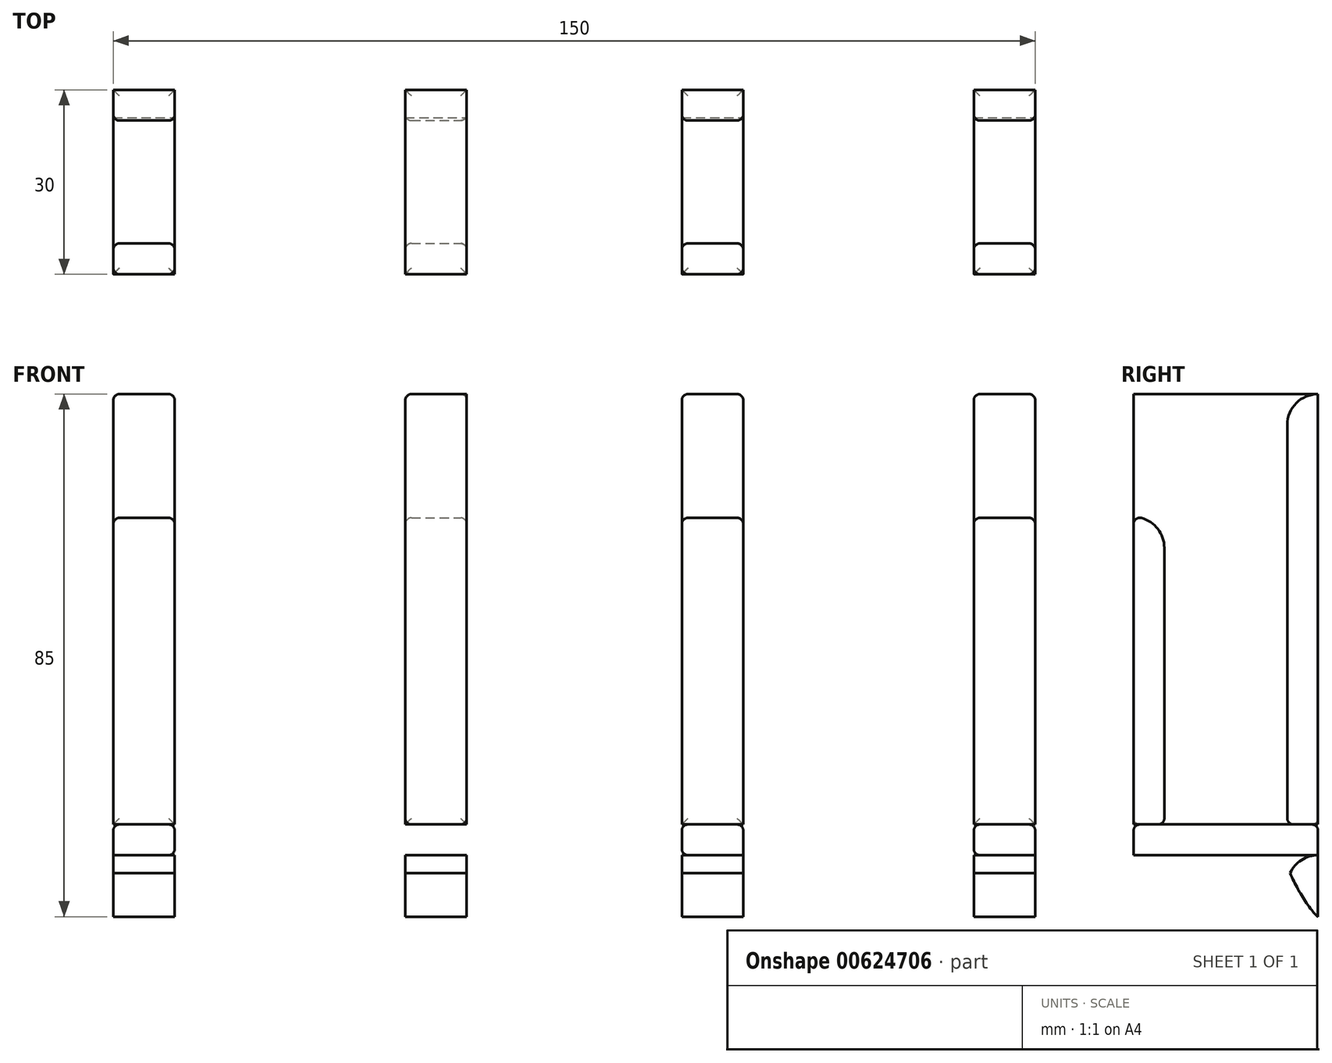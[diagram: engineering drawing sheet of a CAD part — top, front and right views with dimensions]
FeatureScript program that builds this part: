
annotation { "Feature Type Name" : "Feature", "Feature Type Description" : "" }
export const myFeature = defineFeature(function(context is Context, id is Id, definition is map)
    precondition{}
    {
        {
            var Q0;
            Q0=qCreatedBy(makeId("Front.planeOp"),FACE);
            var sketch = newSketch(context, id + "F0", { "sketchPlane" : qUnion([Q0])});
            skLineSegment(sketch, "E0.bottom", {"start": v(-75, 75) * mm, "end": v(-65, 75) * mm});
            skLineSegment(sketch, "E0.top", {"start": v(-75, 0) * mm, "end": v(-65, 0) * mm});
            skLineSegment(sketch, "E0.left", {"start": v(-75, 75) * mm, "end": v(-75, 0) * mm});
            skLineSegment(sketch, "E0.right", {"start": v(-65, 75) * mm, "end": v(-65, 0) * mm});
            skLineSegment(sketch, "E1.bottom", {"start": v(-27.5, 75) * mm, "end": v(-17.5, 75) * mm});
            skLineSegment(sketch, "E1.top", {"start": v(-27.5, 0) * mm, "end": v(-17.5, 0) * mm});
            skLineSegment(sketch, "E1.left", {"start": v(-27.5, 75) * mm, "end": v(-27.5, 0) * mm});
            skLineSegment(sketch, "E1.right", {"start": v(-17.5, 75) * mm, "end": v(-17.5, 0) * mm});
            skLineSegment(sketch, "E2.bottom", {"start": v(17.5, 75) * mm, "end": v(27.5, 75) * mm});
            skLineSegment(sketch, "E2.top", {"start": v(17.5, 0) * mm, "end": v(27.5, 0) * mm});
            skLineSegment(sketch, "E2.left", {"start": v(17.5, 75) * mm, "end": v(17.5, 0) * mm});
            skLineSegment(sketch, "E2.right", {"start": v(27.5, 75) * mm, "end": v(27.5, 0) * mm});
            skLineSegment(sketch, "E3.bottom", {"start": v(65, 75) * mm, "end": v(75, 75) * mm});
            skLineSegment(sketch, "E3.top", {"start": v(65, 0) * mm, "end": v(75, 0) * mm});
            skLineSegment(sketch, "E3.left", {"start": v(65, 75) * mm, "end": v(65, 0) * mm});
            skLineSegment(sketch, "E3.right", {"start": v(75, 75) * mm, "end": v(75, 0) * mm});
            skLineSegment(sketch, "E4", {"start": v(-75, 0) * mm, "end": v(75, 0) * mm});
            skLineSegment(sketch, "E5", {"start": v(-75, 0) * mm, "end": v(0, 0) * mm});
            skLineSegment(sketch, "E6", {"start": v(-65, 0) * mm, "end": v(-27.5, 0) * mm});
            skLineSegment(sketch, "E7", {"start": v(-75, 5) * mm, "end": v(75, 5) * mm});
            skLineSegment(sketch, "E8.top", {"start": v(-75, -10) * mm, "end": v(-65, -10) * mm});
            skLineSegment(sketch, "E8.left", {"start": v(-75, 0) * mm, "end": v(-75, -10) * mm});
            skLineSegment(sketch, "E8.right", {"start": v(-65, 0) * mm, "end": v(-65, -10) * mm});
            skLineSegment(sketch, "E9.top", {"start": v(-27.5, -10) * mm, "end": v(-17.5, -10) * mm});
            skLineSegment(sketch, "E9.left", {"start": v(-27.5, 0) * mm, "end": v(-27.5, -10) * mm});
            skLineSegment(sketch, "E9.right", {"start": v(-17.5, 0) * mm, "end": v(-17.5, -10) * mm});
            skLineSegment(sketch, "E10.top", {"start": v(17.5, -10) * mm, "end": v(27.5, -10) * mm});
            skLineSegment(sketch, "E10.left", {"start": v(17.5, 0) * mm, "end": v(17.5, -10) * mm});
            skLineSegment(sketch, "E10.right", {"start": v(27.5, 0) * mm, "end": v(27.5, -10) * mm});
            skLineSegment(sketch, "E11.top", {"start": v(65, -10) * mm, "end": v(75, -10) * mm});
            skLineSegment(sketch, "E11.left", {"start": v(65, 0) * mm, "end": v(65, -10) * mm});
            skLineSegment(sketch, "E11.right", {"start": v(75, 0) * mm, "end": v(75, -10) * mm});
            skSolve(sketch);
        }
        {
            var Q0;
            Q0=makeQuery(id+"F0.imprint","IMPRINT",FACE,{"disambiguationData":[TD([[makeQuery(id+"F0.imprint","IMPRINT",EDGE,{"derivedFrom":sQuery(id+"F0.wireOp",EDGE,"E0.bottom")}),-1.0]])]});
            var Q1;
            Q1=makeQuery(id+"F0.imprint","IMPRINT",FACE,{"disambiguationData":[TD([[makeQuery(id+"F0.imprint","IMPRINT",EDGE,{"derivedFrom":sQuery(id+"F0.wireOp",EDGE,"E1.bottom")}),-1.0]])]});
            var Q2;
            Q2=makeQuery(id+"F0.imprint","IMPRINT",FACE,{"disambiguationData":[TD([[makeQuery(id+"F0.imprint","IMPRINT",EDGE,{"derivedFrom":sQuery(id+"F0.wireOp",EDGE,"E2.bottom")}),-1.0]])]});
            var Q3;
            Q3=makeQuery(id+"F0.imprint","IMPRINT",FACE,{"disambiguationData":[TD([[makeQuery(id+"F0.imprint","IMPRINT",EDGE,{"derivedFrom":sQuery(id+"F0.wireOp",EDGE,"E3.bottom")}),-1.0]])]});
            var Q4;
            Q4=makeQuery(id+"F0.imprint","IMPRINT",FACE,{"disambiguationData":[TD([[makeQuery(id+"F0.imprint","IMPRINT",EDGE,{"derivedFrom":sQuery(id+"F0.wireOp",EDGE,"E0.top")}),-1.0]])]});
            var Q5;
            Q5=makeQuery(id+"F0.imprint","IMPRINT",FACE,{"disambiguationData":[TD([[makeQuery(id+"F0.imprint","IMPRINT",EDGE,{"derivedFrom":sQuery(id+"F0.wireOp",EDGE,"E1.top")}),-1.0]])]});
            var Q6;
            Q6=makeQuery(id+"F0.imprint","IMPRINT",FACE,{"disambiguationData":[TD([[makeQuery(id+"F0.imprint","IMPRINT",EDGE,{"derivedFrom":sQuery(id+"F0.wireOp",EDGE,"E2.top")}),-1.0]])]});
            var Q7;
            Q7=makeQuery(id+"F0.imprint","IMPRINT",FACE,{"disambiguationData":[TD([[makeQuery(id+"F0.imprint","IMPRINT",EDGE,{"derivedFrom":sQuery(id+"F0.wireOp",EDGE,"E3.top")}),-1.0]])]});
            extrude(context, id + "F1", {"entities" : qUnion([Q0, Q1, Q2, Q3, Q4, Q5, Q6, Q7]), "depth" : 5 * mm, "offsetDistance" : 25 * mm});
        }
        {
            var Q0;
            {var subQ0=sQuery(id+"F0.wireOp",EDGE,"E5");var subQ5=sQuery(id+"F0.wireOp",EDGE,"E1.right");var subQ6=makeQuery(id+"F0.imprint","INTERSECT",VERTEX,{"derivedFrom":[subQ5,subQ0]});Q0=makeQuery(id+"F0.imprint","IMPRINT",FACE,{"disambiguationData":[TD([[makeQuery(id+"F0.imprint","IMPRINT",EDGE,{"disambiguationData":[TD([[subQ6,1.0]])],"derivedFrom":subQ5}),-1.0]])]});}
            var Q1;
            {var subQ0=sQuery(id+"F0.wireOp",EDGE,"E4");var subQ1=sQuery(id+"F0.wireOp",EDGE,"E2.left");var subQ2=makeQuery(id+"F0.imprint","INTERSECT",VERTEX,{"derivedFrom":[subQ1,subQ0]});Q1=makeQuery(id+"F0.imprint","IMPRINT",FACE,{"disambiguationData":[TD([[makeQuery(id+"F0.imprint","IMPRINT",EDGE,{"disambiguationData":[TD([[subQ2,1.0]])],"derivedFrom":subQ1}),1.0]])]});}
            var Q2;
            {var subQ0=sQuery(id+"F0.wireOp",EDGE,"E4");var subQ1=sQuery(id+"F0.wireOp",EDGE,"E3.left");var subQ2=makeQuery(id+"F0.imprint","INTERSECT",VERTEX,{"derivedFrom":[subQ1,subQ0]});Q2=makeQuery(id+"F0.imprint","IMPRINT",FACE,{"disambiguationData":[TD([[makeQuery(id+"F0.imprint","IMPRINT",EDGE,{"disambiguationData":[TD([[subQ2,1.0]])],"derivedFrom":subQ1}),1.0]])]});}
            var Q3;
            {var subQ0=sQuery(id+"F0.wireOp",EDGE,"E0.top");Q3=makeQuery(id+"F0.imprint","IMPRINT",FACE,{"disambiguationData":[TD([[makeQuery(id+"F0.imprint","IMPRINT",EDGE,{"derivedFrom":subQ0}),1.0]])]});}
            extrude(context, id + "F2", {"entities" : qUnion([Q0, Q1, Q2, Q3]), "depth" : (5 + 20 + 5) * mm, "offsetDistance" : 25 * mm});
        }
        {
            var Q0;
            {var subQ0=sQuery(id+"F0.wireOp",EDGE,"E7");Q0=makeQuery(id+"F2.opExtrude","SWEPT_FACE",FACE,{"disambiguationData":[OSD([subQ0]),TDD([makeQuery(id+"F0.imprint","IMPRINT",EDGE,{"disambiguationData":[TD([[makeQuery(id+"F0.imprint","INTERSECT",VERTEX,{"derivedFrom":[sQuery(id+"F0.wireOp",EDGE,"E0.left"),subQ0]}),-1.0]])],"derivedFrom":subQ0})])]});}
            var sketch = newSketch(context, id + "F3", { "sketchPlane" : qUnion([Q0])});
            skLineSegment(sketch, "E12.bottom", {"start": v(-27.5, -25) * mm, "end": v(-17.5, -25) * mm});
            skLineSegment(sketch, "E12.top", {"start": v(-27.5, -30) * mm, "end": v(-17.5, -30) * mm});
            skLineSegment(sketch, "E12.left", {"start": v(-27.5, -25) * mm, "end": v(-27.5, -30) * mm});
            skLineSegment(sketch, "E12.right", {"start": v(-17.5, -25) * mm, "end": v(-17.5, -30) * mm});
            skLineSegment(sketch, "E13.bottom", {"start": v(17.5, -25) * mm, "end": v(27.5, -25) * mm});
            skLineSegment(sketch, "E13.top", {"start": v(17.5, -30) * mm, "end": v(27.5, -30) * mm});
            skLineSegment(sketch, "E13.left", {"start": v(17.5, -25) * mm, "end": v(17.5, -30) * mm});
            skLineSegment(sketch, "E13.right", {"start": v(27.5, -25) * mm, "end": v(27.5, -30) * mm});
            skLineSegment(sketch, "E14.bottom", {"start": v(65, -25) * mm, "end": v(75, -25) * mm});
            skLineSegment(sketch, "E14.top", {"start": v(65, -30) * mm, "end": v(75, -30) * mm});
            skLineSegment(sketch, "E14.left", {"start": v(65, -25) * mm, "end": v(65, -30) * mm});
            skLineSegment(sketch, "E14.right", {"start": v(75, -25) * mm, "end": v(75, -30) * mm});
            skLineSegment(sketch, "E15.bottom", {"start": v(-75, -30) * mm, "end": v(-65, -30) * mm});
            skLineSegment(sketch, "E15.top", {"start": v(-75, -25) * mm, "end": v(-65, -25) * mm});
            skLineSegment(sketch, "E15.left", {"start": v(-75, -30) * mm, "end": v(-75, -25) * mm});
            skLineSegment(sketch, "E15.right", {"start": v(-65, -30) * mm, "end": v(-65, -25) * mm});
            skSolve(sketch);
        }
        {
            var Q0;
            Q0 = qSketchRegion(id + "F3", true);
            extrude(context, id + "F4", {"entities" : qUnion([Q0]), "depth" : 50 * mm, "offsetDistance" : 25 * mm});
        }
        {
            var Q0;
            Q0=makeQuery(id+"F1.opExtrude","SWEPT_BODY",BODY,{"disambiguationData":[OSD([sQuery(id+"F0.wireOp",EDGE,"E0.bottom"),sQuery(id+"F0.wireOp",EDGE,"E0.left"),sQuery(id+"F0.wireOp",EDGE,"E0.right"),sQuery(id+"F0.wireOp",EDGE,"E7")])]});
            var Q1;
            Q1=makeQuery(id+"F1.opExtrude","SWEPT_BODY",BODY,{"disambiguationData":[OSD([sQuery(id+"F0.wireOp",EDGE,"E1.bottom"),sQuery(id+"F0.wireOp",EDGE,"E1.left"),sQuery(id+"F0.wireOp",EDGE,"E1.right"),sQuery(id+"F0.wireOp",EDGE,"E7")])]});
            var Q2;
            Q2=makeQuery(id+"F1.opExtrude","SWEPT_BODY",BODY,{"disambiguationData":[OSD([sQuery(id+"F0.wireOp",EDGE,"E2.bottom"),sQuery(id+"F0.wireOp",EDGE,"E2.left"),sQuery(id+"F0.wireOp",EDGE,"E2.right"),sQuery(id+"F0.wireOp",EDGE,"E7")])]});
            var Q3;
            Q3=makeQuery(id+"F1.opExtrude","SWEPT_BODY",BODY,{"disambiguationData":[OSD([sQuery(id+"F0.wireOp",EDGE,"E3.bottom"),sQuery(id+"F0.wireOp",EDGE,"E3.left"),sQuery(id+"F0.wireOp",EDGE,"E3.right"),sQuery(id+"F0.wireOp",EDGE,"E7")])]});
            var Q4;
            Q4=makeQuery(id+"F4.opExtrude","SWEPT_BODY",BODY,{"disambiguationData":[OSD([sQuery(id+"F3.wireOp",EDGE,"E12.bottom"),sQuery(id+"F3.wireOp",EDGE,"E12.top"),sQuery(id+"F3.wireOp",EDGE,"E12.left"),sQuery(id+"F3.wireOp",EDGE,"E12.right")])]});
            var Q5;
            Q5=makeQuery(id+"F4.opExtrude","SWEPT_BODY",BODY,{"disambiguationData":[OSD([sQuery(id+"F3.wireOp",EDGE,"E13.bottom"),sQuery(id+"F3.wireOp",EDGE,"E13.top"),sQuery(id+"F3.wireOp",EDGE,"E13.left"),sQuery(id+"F3.wireOp",EDGE,"E13.right")])]});
            var Q6;
            Q6=makeQuery(id+"F4.opExtrude","SWEPT_BODY",BODY,{"disambiguationData":[OSD([sQuery(id+"F3.wireOp",EDGE,"E14.bottom"),sQuery(id+"F3.wireOp",EDGE,"E14.top"),sQuery(id+"F3.wireOp",EDGE,"E14.left"),sQuery(id+"F3.wireOp",EDGE,"E14.right")])]});
            var Q7;
            Q7=makeQuery(id+"F4.opExtrude","SWEPT_BODY",BODY,{"disambiguationData":[OSD([sQuery(id+"F3.wireOp",EDGE,"E15.bottom"),sQuery(id+"F3.wireOp",EDGE,"E15.top"),sQuery(id+"F3.wireOp",EDGE,"E15.left"),sQuery(id+"F3.wireOp",EDGE,"E15.right")])]});
            booleanBodies(context, id + "F5", {"operationType" : BooleanOperationType.UNION, "tools" : qUnion([Q0, Q1, Q2, Q3, Q4, Q5, Q6, Q7])});
        }
        {
            var Q0;
            Q0=makeQuery(id+"F1.opExtrude","CAP_EDGE",EDGE,{"disambiguationData":[OSD([sQuery(id+"F0.wireOp",EDGE,"E0.bottom")])],"isStart":false});
            var Q1;
            Q1=makeQuery(id+"F1.opExtrude","CAP_EDGE",EDGE,{"disambiguationData":[OSD([sQuery(id+"F0.wireOp",EDGE,"E1.bottom")])],"isStart":false});
            var Q2;
            Q2=makeQuery(id+"F1.opExtrude","CAP_EDGE",EDGE,{"disambiguationData":[OSD([sQuery(id+"F0.wireOp",EDGE,"E2.bottom")])],"isStart":false});
            var Q3;
            Q3=makeQuery(id+"F1.opExtrude","CAP_EDGE",EDGE,{"disambiguationData":[OSD([sQuery(id+"F0.wireOp",EDGE,"E3.bottom")])],"isStart":false});
            fillet(context, id + "F6", {"entities" : qUnion([Q0, Q1, Q2, Q3]), "radius" : 5 * mm, "tangentPropagation" : true, "allowEdgeOverflow" : false});
        }
        {
            var Q0;
            Q0=makeQuery(id+"F4.opExtrude","CAP_EDGE",EDGE,{"disambiguationData":[OSD([sQuery(id+"F3.wireOp",EDGE,"E15.top")])],"isStart":false});
            var Q1;
            Q1=makeQuery(id+"F4.opExtrude","CAP_EDGE",EDGE,{"disambiguationData":[OSD([sQuery(id+"F3.wireOp",EDGE,"E12.bottom")])],"isStart":false});
            var Q2;
            Q2=makeQuery(id+"F4.opExtrude","CAP_EDGE",EDGE,{"disambiguationData":[OSD([sQuery(id+"F3.wireOp",EDGE,"E13.bottom")])],"isStart":false});
            var Q3;
            Q3=makeQuery(id+"F4.opExtrude","CAP_EDGE",EDGE,{"disambiguationData":[OSD([sQuery(id+"F3.wireOp",EDGE,"E14.bottom")])],"isStart":false});
            fillet(context, id + "F7", {"entities" : qUnion([Q0, Q1, Q2, Q3]), "radius" : 5 * mm, "tangentPropagation" : true, "allowEdgeOverflow" : false});
        }
        {
            var Q0;
            Q0=makeQuery(id+"F7.opFillet","BLEND_EDGE",EDGE,{"blendedFrom":[makeQuery(id+"F4.opExtrude","CAP_EDGE",EDGE,{"disambiguationData":[OSD([sQuery(id+"F3.wireOp",EDGE,"E14.bottom")])],"isStart":false}),makeQuery(id+"F5.opBoolean","MERGE",FACE,{"derivedFrom":[makeQuery(id+"F2.opExtrude","CAP_FACE",FACE,{"disambiguationData":[OSD([sQuery(id+"F0.wireOp",EDGE,"E3.left"),sQuery(id+"F0.wireOp",EDGE,"E3.right"),sQuery(id+"F0.wireOp",EDGE,"E4"),sQuery(id+"F0.wireOp",EDGE,"E7")])],"isStart":false}),makeQuery(id+"F4.opExtrude","SWEPT_FACE",FACE,{"disambiguationData":[OSD([sQuery(id+"F3.wireOp",EDGE,"E14.top")])]})]})],"blendedInto":[makeQuery(id+"F5.opBoolean","MERGE",FACE,{"derivedFrom":[makeQuery(id+"F2.opExtrude","CAP_FACE",FACE,{"disambiguationData":[OSD([sQuery(id+"F0.wireOp",EDGE,"E3.left"),sQuery(id+"F0.wireOp",EDGE,"E3.right"),sQuery(id+"F0.wireOp",EDGE,"E4"),sQuery(id+"F0.wireOp",EDGE,"E7")])],"isStart":false}),makeQuery(id+"F4.opExtrude","SWEPT_FACE",FACE,{"disambiguationData":[OSD([sQuery(id+"F3.wireOp",EDGE,"E14.top")])]})]})]});
            var Q1;
            Q1=makeQuery(id+"F7.opFillet","BLEND_EDGE",EDGE,{"blendedFrom":[makeQuery(id+"F4.opExtrude","CAP_EDGE",EDGE,{"disambiguationData":[OSD([sQuery(id+"F3.wireOp",EDGE,"E13.bottom")])],"isStart":false}),makeQuery(id+"F5.opBoolean","MERGE",FACE,{"derivedFrom":[makeQuery(id+"F2.opExtrude","CAP_FACE",FACE,{"disambiguationData":[OSD([sQuery(id+"F0.wireOp",EDGE,"E2.left"),sQuery(id+"F0.wireOp",EDGE,"E2.right"),sQuery(id+"F0.wireOp",EDGE,"E4"),sQuery(id+"F0.wireOp",EDGE,"E7")])],"isStart":false}),makeQuery(id+"F4.opExtrude","SWEPT_FACE",FACE,{"disambiguationData":[OSD([sQuery(id+"F3.wireOp",EDGE,"E13.top")])]})]})],"blendedInto":[makeQuery(id+"F5.opBoolean","MERGE",FACE,{"derivedFrom":[makeQuery(id+"F2.opExtrude","CAP_FACE",FACE,{"disambiguationData":[OSD([sQuery(id+"F0.wireOp",EDGE,"E2.left"),sQuery(id+"F0.wireOp",EDGE,"E2.right"),sQuery(id+"F0.wireOp",EDGE,"E4"),sQuery(id+"F0.wireOp",EDGE,"E7")])],"isStart":false}),makeQuery(id+"F4.opExtrude","SWEPT_FACE",FACE,{"disambiguationData":[OSD([sQuery(id+"F3.wireOp",EDGE,"E13.top")])]})]})]});
            var Q2;
            Q2=makeQuery(id+"F7.opFillet","BLEND_EDGE",EDGE,{"blendedFrom":[makeQuery(id+"F4.opExtrude","CAP_EDGE",EDGE,{"disambiguationData":[OSD([sQuery(id+"F3.wireOp",EDGE,"E15.top")])],"isStart":false}),makeQuery(id+"F5.opBoolean","MERGE",FACE,{"derivedFrom":[makeQuery(id+"F2.opExtrude","CAP_FACE",FACE,{"disambiguationData":[OSD([sQuery(id+"F0.wireOp",EDGE,"E0.left"),sQuery(id+"F0.wireOp",EDGE,"E0.right"),sQuery(id+"F0.wireOp",EDGE,"E5"),sQuery(id+"F0.wireOp",EDGE,"E7")])],"isStart":false}),makeQuery(id+"F4.opExtrude","SWEPT_FACE",FACE,{"disambiguationData":[OSD([sQuery(id+"F3.wireOp",EDGE,"E15.bottom")])]})]})],"blendedInto":[makeQuery(id+"F5.opBoolean","MERGE",FACE,{"derivedFrom":[makeQuery(id+"F2.opExtrude","CAP_FACE",FACE,{"disambiguationData":[OSD([sQuery(id+"F0.wireOp",EDGE,"E0.left"),sQuery(id+"F0.wireOp",EDGE,"E0.right"),sQuery(id+"F0.wireOp",EDGE,"E5"),sQuery(id+"F0.wireOp",EDGE,"E7")])],"isStart":false}),makeQuery(id+"F4.opExtrude","SWEPT_FACE",FACE,{"disambiguationData":[OSD([sQuery(id+"F3.wireOp",EDGE,"E15.bottom")])]})]})]});
            var Q3;
            Q3=makeQuery(id+"F7.opFillet","BLEND_EDGE",EDGE,{"blendedFrom":[makeQuery(id+"F4.opExtrude","CAP_EDGE",EDGE,{"disambiguationData":[OSD([sQuery(id+"F3.wireOp",EDGE,"E12.bottom")])],"isStart":false}),makeQuery(id+"F5.opBoolean","MERGE",FACE,{"derivedFrom":[makeQuery(id+"F2.opExtrude","CAP_FACE",FACE,{"disambiguationData":[OSD([sQuery(id+"F0.wireOp",EDGE,"E1.left"),sQuery(id+"F0.wireOp",EDGE,"E1.right"),sQuery(id+"F0.wireOp",EDGE,"E5"),sQuery(id+"F0.wireOp",EDGE,"E7")])],"isStart":false}),makeQuery(id+"F4.opExtrude","SWEPT_FACE",FACE,{"disambiguationData":[OSD([sQuery(id+"F3.wireOp",EDGE,"E12.top")])]})]})],"blendedInto":[makeQuery(id+"F5.opBoolean","MERGE",FACE,{"derivedFrom":[makeQuery(id+"F2.opExtrude","CAP_FACE",FACE,{"disambiguationData":[OSD([sQuery(id+"F0.wireOp",EDGE,"E1.left"),sQuery(id+"F0.wireOp",EDGE,"E1.right"),sQuery(id+"F0.wireOp",EDGE,"E5"),sQuery(id+"F0.wireOp",EDGE,"E7")])],"isStart":false}),makeQuery(id+"F4.opExtrude","SWEPT_FACE",FACE,{"disambiguationData":[OSD([sQuery(id+"F3.wireOp",EDGE,"E12.top")])]})]})]});
            fillet(context, id + "F8", {"entities" : qUnion([Q0, Q1, Q2, Q3]), "radius" : 1 * mm, "tangentPropagation" : true, "allowEdgeOverflow" : false});
        }
        {
            var Q0;
            Q0=makeQuery(id+"F1.opExtrude","CAP_EDGE",EDGE,{"disambiguationData":[OSD([sQuery(id+"F0.wireOp",EDGE,"E1.left")])],"isStart":false});
            var Q1;
            Q1=makeQuery(id+"F1.opExtrude","CAP_EDGE",EDGE,{"disambiguationData":[OSD([sQuery(id+"F0.wireOp",EDGE,"E0.left")])],"isStart":false});
            var Q2;
            Q2=makeQuery(id+"F1.opExtrude","CAP_EDGE",EDGE,{"disambiguationData":[OSD([sQuery(id+"F0.wireOp",EDGE,"E2.left")])],"isStart":false});
            var Q3;
            Q3=makeQuery(id+"F1.opExtrude","CAP_EDGE",EDGE,{"disambiguationData":[OSD([sQuery(id+"F0.wireOp",EDGE,"E3.left")])],"isStart":false});
            var Q4;
            Q4=makeQuery(id+"F1.opExtrude","CAP_EDGE",EDGE,{"disambiguationData":[OSD([sQuery(id+"F0.wireOp",EDGE,"E1.right")])],"isStart":false});
            var Q5;
            Q5=makeQuery(id+"F1.opExtrude","CAP_EDGE",EDGE,{"disambiguationData":[OSD([sQuery(id+"F0.wireOp",EDGE,"E0.right")])],"isStart":false});
            var Q6;
            Q6=makeQuery(id+"F1.opExtrude","CAP_EDGE",EDGE,{"disambiguationData":[OSD([sQuery(id+"F0.wireOp",EDGE,"E2.right")])],"isStart":false});
            var Q7;
            Q7=makeQuery(id+"F1.opExtrude","CAP_EDGE",EDGE,{"disambiguationData":[OSD([sQuery(id+"F0.wireOp",EDGE,"E3.right")])],"isStart":false});
            var Q8;
            {var subQ0=sQuery(id+"F0.wireOp",EDGE,"E7");Q8=makeQuery(id+"F2.opExtrude","SWEPT_FACE",FACE,{"disambiguationData":[OSD([subQ0]),TDD([makeQuery(id+"F0.imprint","IMPRINT",EDGE,{"disambiguationData":[TD([[makeQuery(id+"F0.imprint","INTERSECT",VERTEX,{"derivedFrom":[sQuery(id+"F0.wireOp",EDGE,"E1.left"),subQ0]}),-1.0]])],"derivedFrom":subQ0})])]});}
            var Q9;
            {var subQ0=sQuery(id+"F0.wireOp",EDGE,"E7");Q9=makeQuery(id+"F2.opExtrude","SWEPT_FACE",FACE,{"disambiguationData":[OSD([subQ0]),TDD([makeQuery(id+"F0.imprint","IMPRINT",EDGE,{"disambiguationData":[TD([[makeQuery(id+"F0.imprint","INTERSECT",VERTEX,{"derivedFrom":[sQuery(id+"F0.wireOp",EDGE,"E2.left"),subQ0]}),-1.0]])],"derivedFrom":subQ0})])]});}
            var Q10;
            {var subQ0=sQuery(id+"F0.wireOp",EDGE,"E7");Q10=makeQuery(id+"F2.opExtrude","SWEPT_FACE",FACE,{"disambiguationData":[OSD([subQ0]),TDD([makeQuery(id+"F0.imprint","IMPRINT",EDGE,{"disambiguationData":[TD([[makeQuery(id+"F0.imprint","INTERSECT",VERTEX,{"derivedFrom":[sQuery(id+"F0.wireOp",EDGE,"E3.right"),subQ0]}),1.0]])],"derivedFrom":subQ0})])]});}
            var Q11;
            Q11=makeQuery(id+"F1.opExtrude","CAP_FACE",FACE,{"disambiguationData":[OSD([sQuery(id+"F0.wireOp",EDGE,"E3.bottom"),sQuery(id+"F0.wireOp",EDGE,"E3.left"),sQuery(id+"F0.wireOp",EDGE,"E3.right"),sQuery(id+"F0.wireOp",EDGE,"E7")])],"isStart":false});
            var Q12;
            Q12=makeQuery(id+"F1.opExtrude","CAP_FACE",FACE,{"disambiguationData":[OSD([sQuery(id+"F0.wireOp",EDGE,"E2.bottom"),sQuery(id+"F0.wireOp",EDGE,"E2.left"),sQuery(id+"F0.wireOp",EDGE,"E2.right"),sQuery(id+"F0.wireOp",EDGE,"E7")])],"isStart":false});
            var Q13;
            Q13=makeQuery(id+"F1.opExtrude","CAP_FACE",FACE,{"disambiguationData":[OSD([sQuery(id+"F0.wireOp",EDGE,"E1.bottom"),sQuery(id+"F0.wireOp",EDGE,"E1.left"),sQuery(id+"F0.wireOp",EDGE,"E1.right"),sQuery(id+"F0.wireOp",EDGE,"E7")])],"isStart":false});
            var Q14;
            Q14=makeQuery(id+"F1.opExtrude","CAP_FACE",FACE,{"disambiguationData":[OSD([sQuery(id+"F0.wireOp",EDGE,"E0.bottom"),sQuery(id+"F0.wireOp",EDGE,"E0.left"),sQuery(id+"F0.wireOp",EDGE,"E0.right"),sQuery(id+"F0.wireOp",EDGE,"E7")])],"isStart":false});
            var Q15;
            {var subQ0=sQuery(id+"F0.wireOp",EDGE,"E7");Q15=makeQuery(id+"F2.opExtrude","SWEPT_FACE",FACE,{"disambiguationData":[OSD([subQ0]),TDD([makeQuery(id+"F0.imprint","IMPRINT",EDGE,{"disambiguationData":[TD([[makeQuery(id+"F0.imprint","INTERSECT",VERTEX,{"derivedFrom":[sQuery(id+"F0.wireOp",EDGE,"E0.left"),subQ0]}),-1.0]])],"derivedFrom":subQ0})])]});}
            var Q16;
            Q16=makeQuery(id+"F4.opExtrude","SWEPT_FACE",FACE,{"disambiguationData":[OSD([sQuery(id+"F3.wireOp",EDGE,"E15.top")])]});
            var Q17;
            Q17=makeQuery(id+"F4.opExtrude","SWEPT_FACE",FACE,{"disambiguationData":[OSD([sQuery(id+"F3.wireOp",EDGE,"E12.bottom")])]});
            var Q18;
            Q18=makeQuery(id+"F4.opExtrude","SWEPT_FACE",FACE,{"disambiguationData":[OSD([sQuery(id+"F3.wireOp",EDGE,"E13.bottom")])]});
            var Q19;
            Q19=makeQuery(id+"F4.opExtrude","SWEPT_FACE",FACE,{"disambiguationData":[OSD([sQuery(id+"F3.wireOp",EDGE,"E14.bottom")])]});
            fillet(context, id + "F9", {"entities" : qUnion([Q0, Q1, Q2, Q3, Q4, Q5, Q6, Q7, Q8, Q9, Q10, Q11, Q12, Q13, Q14, Q15, Q16, Q17, Q18, Q19]), "radius" : 1 * mm, "tangentPropagation" : true, "allowEdgeOverflow" : false});
        }
        {
            var Q0;
            Q0=makeQuery(id+"F1.opExtrude","CAP_EDGE",EDGE,{"disambiguationData":[OSD([sQuery(id+"F0.wireOp",EDGE,"E8.top")])],"isStart":false});
            var Q1;
            Q1=makeQuery(id+"F1.opExtrude","CAP_EDGE",EDGE,{"disambiguationData":[OSD([sQuery(id+"F0.wireOp",EDGE,"E9.top")])],"isStart":false});
            var Q2;
            Q2=makeQuery(id+"F1.opExtrude","CAP_EDGE",EDGE,{"disambiguationData":[OSD([sQuery(id+"F0.wireOp",EDGE,"E10.top")])],"isStart":false});
            var Q3;
            Q3=makeQuery(id+"F1.opExtrude","CAP_EDGE",EDGE,{"disambiguationData":[OSD([sQuery(id+"F0.wireOp",EDGE,"E11.top")])],"isStart":false});
            fillet(context, id + "F10", {"entities" : qUnion([Q0, Q1, Q2, Q3]), "radius" : 10 * mm, "tangentPropagation" : true, "rho" : .2, "crossSection" : FilletCrossSection.CONIC, "allowEdgeOverflow" : false});
        }
        {
            var Q0;
            Q0=makeQuery(id+"F1.opExtrude","CAP_EDGE",EDGE,{"disambiguationData":[OSD([sQuery(id+"F0.wireOp",EDGE,"E0.top")])],"isStart":false});
            var Q1;
            Q1=makeQuery(id+"F1.opExtrude","CAP_EDGE",EDGE,{"disambiguationData":[OSD([sQuery(id+"F0.wireOp",EDGE,"E1.top")])],"isStart":false});
            var Q2;
            Q2=makeQuery(id+"F1.opExtrude","CAP_EDGE",EDGE,{"disambiguationData":[OSD([sQuery(id+"F0.wireOp",EDGE,"E2.top")])],"isStart":false});
            var Q3;
            Q3=makeQuery(id+"F1.opExtrude","CAP_EDGE",EDGE,{"disambiguationData":[OSD([sQuery(id+"F0.wireOp",EDGE,"E3.top")])],"isStart":false});
            fillet(context, id + "F11", {"entities" : qUnion([Q0, Q1, Q2, Q3]), "radius" : 5 * mm, "tangentPropagation" : true, "allowEdgeOverflow" : false});
        }
        {
            var Q0;
            {var subQ0=sQuery(id+"F0.wireOp",EDGE,"E5");Q0=makeQuery(id+"F2.opExtrude","CAP_EDGE",EDGE,{"disambiguationData":[OSD([subQ0]),TDD([makeQuery(id+"F0.imprint","IMPRINT",EDGE,{"disambiguationData":[TD([[makeQuery(id+"F0.imprint","INTERSECT",VERTEX,{"derivedFrom":[sQuery(id+"F0.wireOp",EDGE,"E0.left"),subQ0]}),-1.0]])],"derivedFrom":subQ0})])],"isStart":false});}
            var Q1;
            {var subQ0=sQuery(id+"F0.wireOp",EDGE,"E5");Q1=makeQuery(id+"F2.opExtrude","CAP_EDGE",EDGE,{"disambiguationData":[OSD([subQ0]),TDD([makeQuery(id+"F0.imprint","IMPRINT",EDGE,{"disambiguationData":[TD([[makeQuery(id+"F0.imprint","INTERSECT",VERTEX,{"derivedFrom":[sQuery(id+"F0.wireOp",EDGE,"E1.right"),subQ0]}),1.0]])],"derivedFrom":subQ0})])],"isStart":false});}
            var Q2;
            {var subQ0=sQuery(id+"F0.wireOp",EDGE,"E4");Q2=makeQuery(id+"F2.opExtrude","CAP_EDGE",EDGE,{"disambiguationData":[OSD([subQ0]),TDD([makeQuery(id+"F0.imprint","IMPRINT",EDGE,{"disambiguationData":[TD([[makeQuery(id+"F0.imprint","INTERSECT",VERTEX,{"derivedFrom":[sQuery(id+"F0.wireOp",EDGE,"E2.left"),subQ0]}),-1.0]])],"derivedFrom":subQ0})])],"isStart":false});}
            var Q3;
            {var subQ0=sQuery(id+"F0.wireOp",EDGE,"E4");Q3=makeQuery(id+"F2.opExtrude","CAP_EDGE",EDGE,{"disambiguationData":[OSD([subQ0]),TDD([makeQuery(id+"F0.imprint","IMPRINT",EDGE,{"disambiguationData":[TD([[makeQuery(id+"F0.imprint","INTERSECT",VERTEX,{"derivedFrom":[sQuery(id+"F0.wireOp",EDGE,"E3.left"),subQ0]}),-1.0]])],"derivedFrom":subQ0})])],"isStart":false});}
            var Q4;
            Q4=makeQuery(id+"F2.opExtrude","SWEPT_EDGE",EDGE,{"disambiguationData":[OSD([sQuery(id+"F0.wireOp",EDGE,"E0.right"),sQuery(id+"F0.wireOp",EDGE,"E6"),sQuery(id+"F0.wireOp",EDGE,"E0.top"),sQuery(id+"F0.wireOp",EDGE,"E8.right")])]});
            var Q5;
            Q5=makeQuery(id+"F2.opExtrude","SWEPT_EDGE",EDGE,{"disambiguationData":[OSD([sQuery(id+"F0.wireOp",EDGE,"E1.left"),sQuery(id+"F0.wireOp",EDGE,"E6"),sQuery(id+"F0.wireOp",EDGE,"E1.top"),sQuery(id+"F0.wireOp",EDGE,"E9.left")])]});
            var Q6;
            Q6=makeQuery(id+"F2.opExtrude","SWEPT_EDGE",EDGE,{"disambiguationData":[OSD([sQuery(id+"F0.wireOp",EDGE,"E2.left"),sQuery(id+"F0.wireOp",EDGE,"E4"),sQuery(id+"F0.wireOp",EDGE,"E2.top"),sQuery(id+"F0.wireOp",EDGE,"E10.left")])]});
            var Q7;
            Q7=makeQuery(id+"F2.opExtrude","SWEPT_EDGE",EDGE,{"disambiguationData":[OSD([sQuery(id+"F0.wireOp",EDGE,"E3.left"),sQuery(id+"F0.wireOp",EDGE,"E4"),sQuery(id+"F0.wireOp",EDGE,"E3.top"),sQuery(id+"F0.wireOp",EDGE,"E11.left")])]});
            fillet(context, id + "F12", {"entities" : qUnion([Q0, Q1, Q2, Q3, Q4, Q5, Q6, Q7]), "radius" : 1 * mm, "tangentPropagation" : true, "allowEdgeOverflow" : false});
        }
    });
